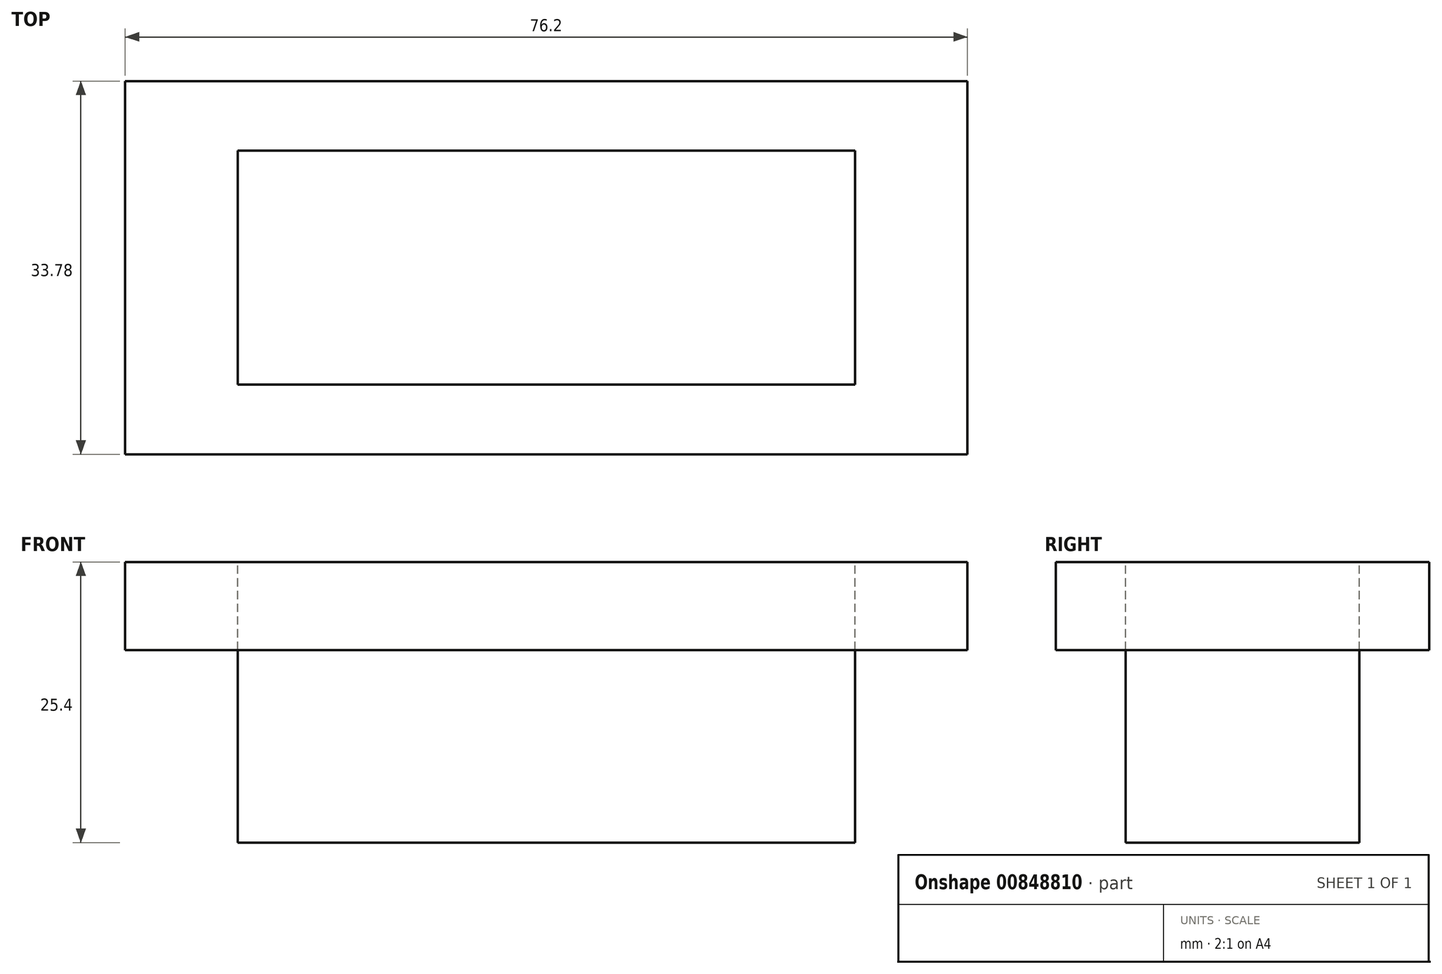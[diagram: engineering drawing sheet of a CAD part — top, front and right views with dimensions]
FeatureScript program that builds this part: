
annotation { "Feature Type Name" : "Feature", "Feature Type Description" : "" }
export const myFeature = defineFeature(function(context is Context, id is Id, definition is map)
    precondition{}
    {
        {
            var Q0;
            Q0=qCreatedBy(makeId("Top.planeOp"),FACE);
            var sketch = newSketch(context, id + "F0", { "sketchPlane" : qUnion([Q0])});
            skLineSegment(sketch, "E0.bottom", {"start": v(38.1, -16.9) * mm, "end": v(-38.1, -16.9) * mm});
            skLineSegment(sketch, "E0.top", {"start": v(38.1, 16.9) * mm, "end": v(-38.1, 16.9) * mm});
            skLineSegment(sketch, "E0.left", {"start": v(38.1, -16.9) * mm, "end": v(38.1, 16.9) * mm});
            skLineSegment(sketch, "E0.right", {"start": v(-38.1, -16.9) * mm, "end": v(-38.1, 16.9) * mm});
            skPoint(sketch, "E0.middle", {"position": v(0, 0) * mm});
            skSolve(sketch);
        }
        {
            var Q0;
            Q0=makeQuery(id+"F0.imprint","IMPRINT",FACE,{"disambiguationData":[TD([[makeQuery(id+"F0.imprint","IMPRINT",EDGE,{"derivedFrom":sQuery(id+"F0.wireOp",EDGE,"E0.bottom")}),-1.0]])]});
            extrude(context, id + "F1", {"entities" : qUnion([Q0]), "oppositeDirection" : true, "depth" : 7.98 * mm, "offsetDistance" : 25.4 * mm});
        }
        {
            var Q0;
            Q0=makeQuery(id+"F1.opExtrude","CAP_FACE",FACE,{"disambiguationData":[OSD([sQuery(id+"F0.wireOp",EDGE,"E0.bottom"),sQuery(id+"F0.wireOp",EDGE,"E0.top"),sQuery(id+"F0.wireOp",EDGE,"E0.left"),sQuery(id+"F0.wireOp",EDGE,"E0.right")])],"isStart":true});
            var sketch = newSketch(context, id + "F2", { "sketchPlane" : qUnion([Q0])});
            skLineSegment(sketch, "E1.bottom", {"start": v(27.92, -10.58) * mm, "end": v(-27.92, -10.58) * mm});
            skLineSegment(sketch, "E1.top", {"start": v(27.92, 10.58) * mm, "end": v(-27.92, 10.58) * mm});
            skLineSegment(sketch, "E1.left", {"start": v(27.92, -10.58) * mm, "end": v(27.92, 10.58) * mm});
            skLineSegment(sketch, "E1.right", {"start": v(-27.92, -10.58) * mm, "end": v(-27.92, 10.58) * mm});
            skPoint(sketch, "E1.middle", {"position": v(0, 0) * mm});
            skSolve(sketch);
        }
        {
            var Q0;
            Q0=makeQuery(id+"F2.imprint","IMPRINT",FACE,{"disambiguationData":[TD([[makeQuery(id+"F2.imprint","IMPRINT",EDGE,{"derivedFrom":sQuery(id+"F2.wireOp",EDGE,"E1.bottom")}),-1.0]])]});
            extrude(context, id + "F3", {"entities" : qUnion([Q0]), "oppositeDirection" : true, "depth" : 25.4 * mm, "offsetDistance" : 25.4 * mm});
        }
    });
